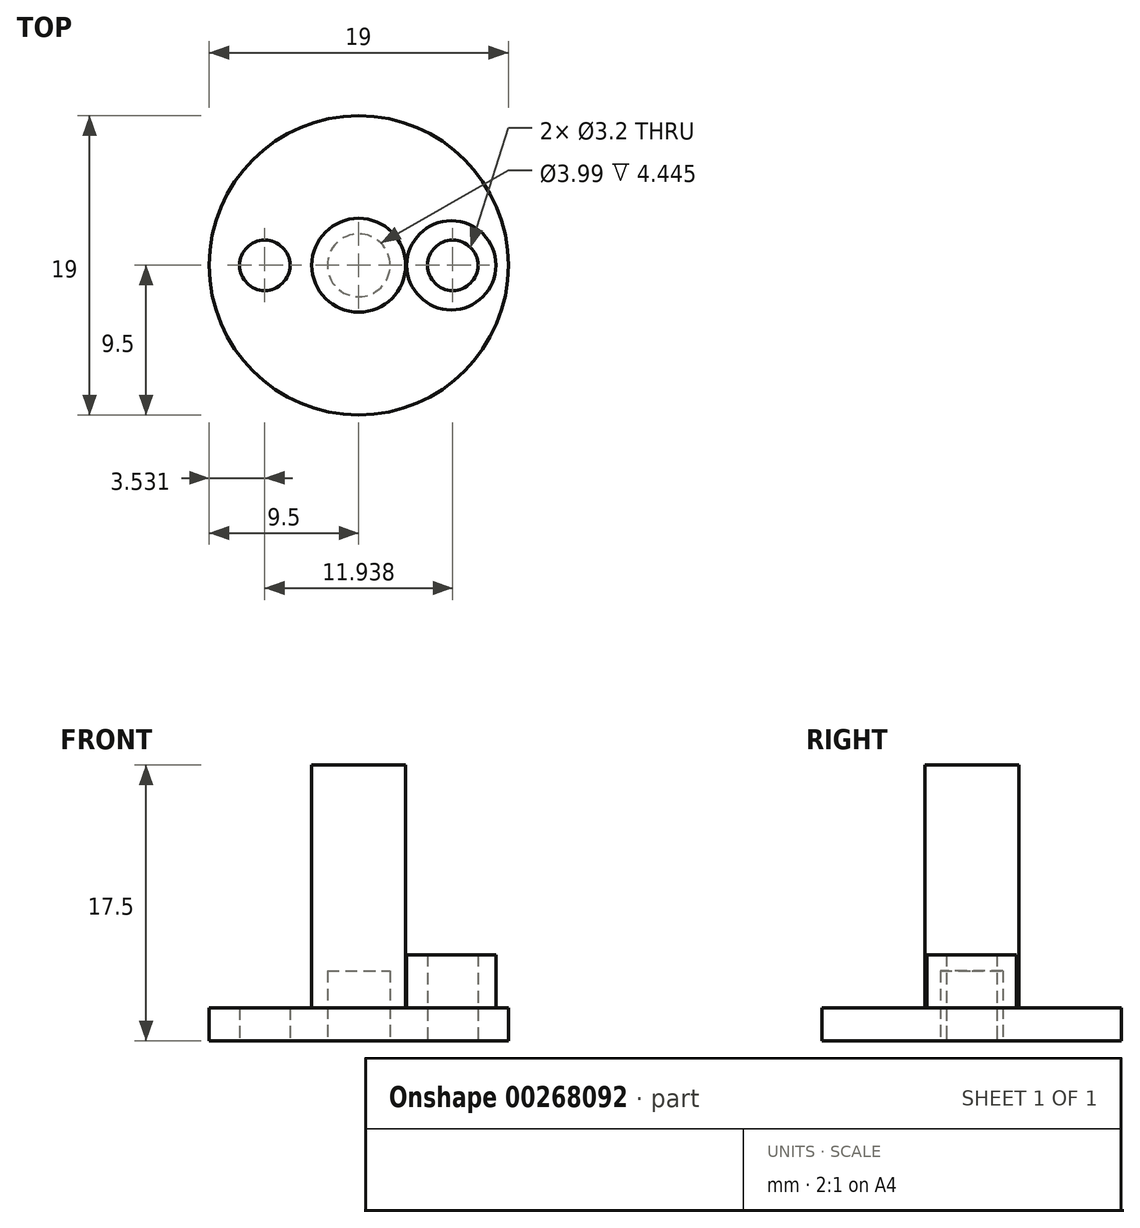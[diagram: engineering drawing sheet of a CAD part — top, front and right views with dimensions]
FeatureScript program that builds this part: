
annotation { "Feature Type Name" : "Feature", "Feature Type Description" : "" }
export const myFeature = defineFeature(function(context is Context, id is Id, definition is map)
    precondition{}
    {
        {
            var Q0;
            Q0=qCreatedBy(makeId("Top.planeOp"),FACE);
            var sketch = newSketch(context, id + "F0", { "sketchPlane" : qUnion([Q0])});
            skCircle(sketch, "E0", {"center": v(0, 0) * mm, "radius": 9.5 * mm});
            skSolve(sketch);
        }
        {
            var Q0;
            Q0 = qSketchRegion(id + "F0", true);
            extrude(context, id + "F1", {"entities" : qUnion([Q0]), "depth" : 5.46 * mm});
        }
        {
            var Q0;
            Q0=makeQuery(id+"F1.opExtrude","CAP_FACE",FACE,{"disambiguationData":[OSD([sQuery(id+"F0.wireOp",EDGE,"E0")])],"isStart":false});
            var sketch = newSketch(context, id + "F2", { "sketchPlane" : qUnion([Q0])});
            skCircle(sketch, "E1", {"center": v(0, 0) * mm, "radius": 2.98 * mm});
            skSolve(sketch);
        }
        {
            var Q0;
            Q0 = qSketchRegion(id + "F2", true);
            extrude(context, id + "F3", {"entities" : qUnion([Q0]), "operationType" : NewBodyOperationType.ADD, "depth" : 12.04 * mm});
        }
        {
            var Q0;
            Q0=makeQuery(id+"F1.opExtrude","CAP_FACE",FACE,{"disambiguationData":[OSD([sQuery(id+"F0.wireOp",EDGE,"E0")])],"isStart":false});
            var sketch = newSketch(context, id + "F4", { "sketchPlane" : qUnion([Q0])});
            skCircle(sketch, "E2", {"center": v(-5.88, 0) * mm, "radius": 2.83 * mm});
            skCircle(sketch, "E3.MirrorC", {"center": v(5.88, 0) * mm, "radius": 2.83 * mm});
            skSolve(sketch);
        }
        {
            var Q0;
            Q0=makeQuery(id+"F4.imprint","IMPRINT",FACE,{"disambiguationData":[TD([[makeQuery(id+"F4.imprint","IMPRINT",EDGE,{"derivedFrom":sQuery(id+"F4.wireOp",EDGE,"E2")}),1.0]])]});
            var Q1;
            Q1=makeQuery(id+"F4.imprint","IMPRINT",FACE,{"disambiguationData":[TD([[makeQuery(id+"F4.imprint","IMPRINT",EDGE,{"derivedFrom":sQuery(id+"F4.wireOp",EDGE,"E3.MirrorC")}),-1.0]])]});
            extrude(context, id + "F5", {"entities" : qUnion([Q0, Q1]), "operationType" : NewBodyOperationType.REMOVE, "oppositeDirection" : true, "depth" : 3.38 * mm});
        }
        {
            var Q0;
            Q0=makeQuery(id+"F1.opExtrude","CAP_FACE",FACE,{"disambiguationData":[OSD([sQuery(id+"F0.wireOp",EDGE,"E0")])],"isStart":true});
            var sketch = newSketch(context, id + "F6", { "sketchPlane" : qUnion([Q0])});
            skCircle(sketch, "E4", {"center": v(0, 0) * mm, "radius": 2 * mm});
            skSolve(sketch);
        }
        {
            var Q0;
            Q0 = qSketchRegion(id + "F6", true);
            extrude(context, id + "F7", {"entities" : qUnion([Q0]), "operationType" : NewBodyOperationType.REMOVE, "oppositeDirection" : true, "depth" : 4.44 * mm});
        }
        {
            var Q0;
            Q0=makeQuery(id+"F1.opExtrude","CAP_FACE",FACE,{"disambiguationData":[OSD([sQuery(id+"F0.wireOp",EDGE,"E0")])],"isStart":true});
            var sketch = newSketch(context, id + "F8", { "sketchPlane" : qUnion([Q0])});
            skCircle(sketch, "E5", {"center": v(5.97, 0) * mm, "radius": 1.6 * mm});
            skCircle(sketch, "E6.MirrorC", {"center": v(-5.97, 0) * mm, "radius": 1.6 * mm});
            skSolve(sketch);
        }
        {
            var Q0;
            Q0 = qSketchRegion(id + "F8", true);
            extrude(context, id + "F9", {"entities" : qUnion([Q0]), "operationType" : NewBodyOperationType.REMOVE, "oppositeDirection" : true, "depth" : 25.4 * mm});
        }
    });
